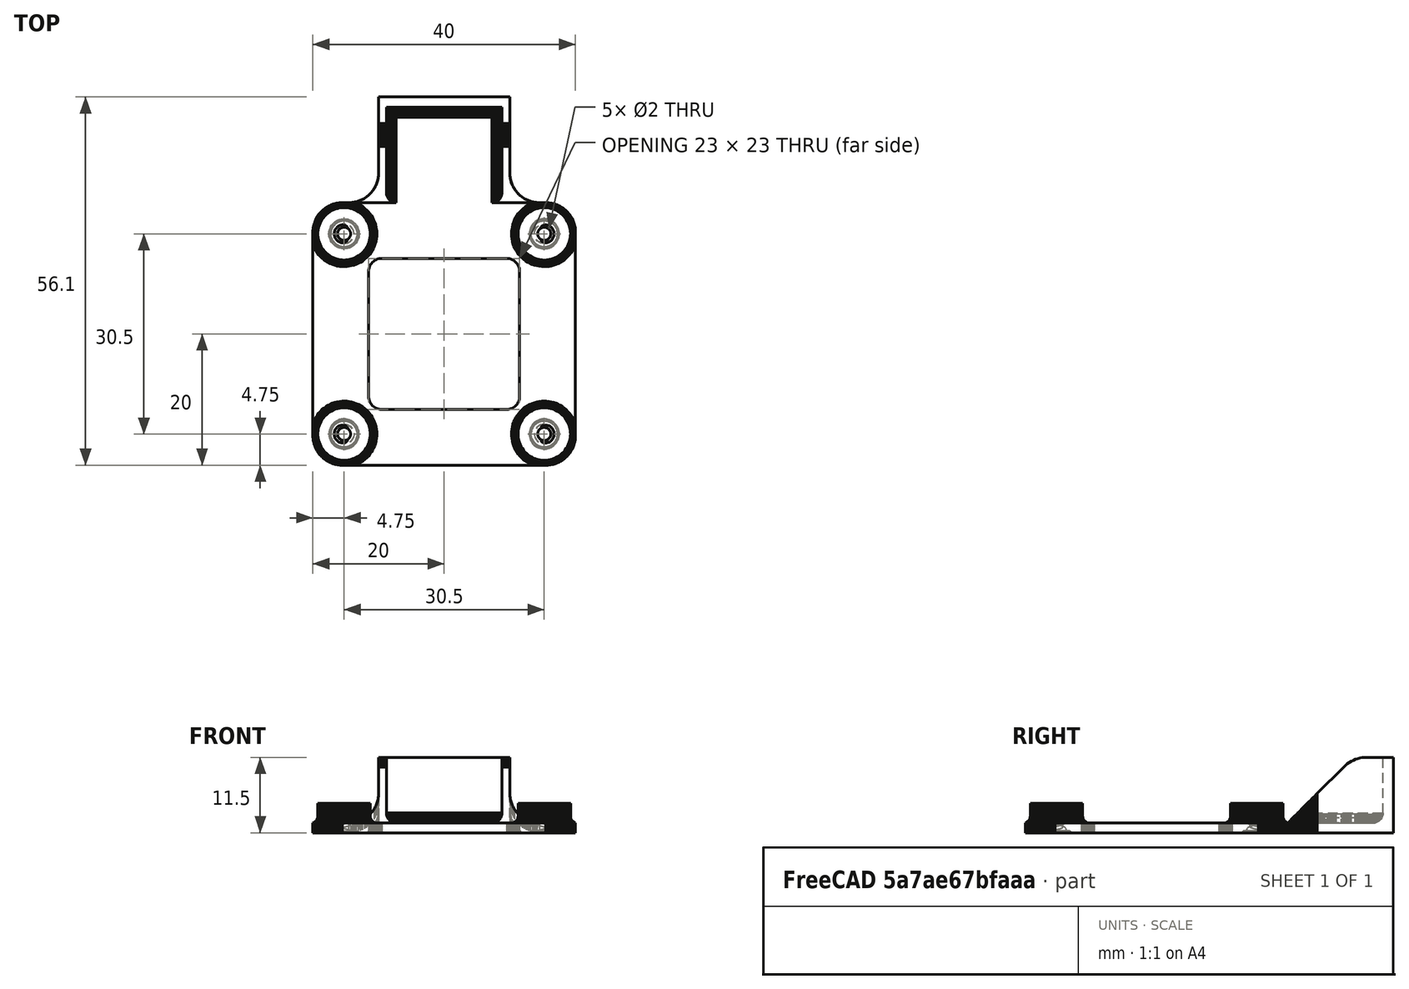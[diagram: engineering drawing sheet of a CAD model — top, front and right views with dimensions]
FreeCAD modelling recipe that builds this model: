
FCSTD DOCUMENT  (FreeCAD 0.21R33694 (Git))
Label: soporte-pdb
License: Creative Commons Attribution-NonCommercial-ShareAlike 4.0
LicenseURL: https://creativecommons.org/licenses/by-nc-sa/4.0/
objects: Part::Fuse×5, Part::Mirroring×4, Part::Feature×2, Part::Cylinder×1, Part::Refine×1, PartDesign::FeatureBase×1, PartDesign::Body×1, Part::Cut×1
note: 16 computed .brp shape members not serialized (recipe doc carries the construction recipe); baked Part::Feature solids carry a one-line shape summary decoded from their .brp

FEATURE [Part::Feature] Fusion001001  label="Rosca macho002"
  Placement = pos=(15.25,-15.25,3) rot=(0,0,1;0rad)
  shape: bbox 3.919 x 4.387 x 44 mm, 35 faces (baked)
FEATURE [Part::Cylinder] Cylinder
  Angle = 360
  AttacherType = Attacher::AttachEngine3D
  FirstAngle = 0
  Height = 4.5
  Placement = pos=(15.25,-15.25,0) rot=(0,0,1;0rad)
  Radius = 2
  SecondAngle = 0
FEATURE [Part::Mirroring] Part__Mirroring  label="Cylinder (Mirror #1)"
  Base = (0,0,0)
  Normal = (0,1,0)
  Source = -> Cylinder
FEATURE [Part::Fuse] Fusion
  Base = -> Cylinder
  Refine = true
  Tool = -> Part__Mirroring
FEATURE [Part::Mirroring] Part__Mirroring001  label="Fusion (Mirror #2)"
  Base = (0,0,0)
  Normal = (1,0,0)
  Source = -> Fusion
FEATURE [Part::Fuse] Fusion001002
  Base = -> Fusion
  Refine = true
  Tool = -> Part__Mirroring001
FEATURE [Part::Feature] base001_solid  label="base001 (Solid)"
  shape: bbox 40 x 56.1 x 11.5 mm, 10680 faces (baked)
FEATURE [Part::Refine] base001_solid001  label="base001 (Solid)001"
  Source = -> base001_solid
FEATURE [PartDesign::FeatureBase] BaseFeature
  BaseFeature = -> base001_solid001
FEATURE [PartDesign::Body] Body
  BaseFeature = -> base001_solid001
  Group = -> [BaseFeature]
  Origin = -> Origin
  Tip = -> BaseFeature
FEATURE [Part::Fuse] Fusion001003  label="soporte-pdb"
  Base = -> Fusion001002
  Refine = true
  Tool = -> Body
FEATURE [Part::Mirroring] Part__Mirroring002  label="Rosca macho002 (Mirror #3)"
  Base = (0,0,0)
  Normal = (0,1,0)
  Source = -> Fusion001001
FEATURE [Part::Fuse] Fusion001004
  Base = -> Fusion001001
  Refine = true
  Tool = -> Part__Mirroring002
FEATURE [Part::Mirroring] Part__Mirroring003  label="Fusion001004 (Mirror #4)"
  Base = (0,0,0)
  Normal = (1,0,0)
  Source = -> Fusion001004
FEATURE [Part::Fuse] Fusion001005
  Base = -> Fusion001004
  Placement = pos=(0,0,-3) rot=(0,0,1;0rad)
  Refine = true
  Tool = -> Part__Mirroring003
FEATURE [Part::Cut] Cut  label="soporte-pdb001"
  Base = -> Fusion001003
  Refine = true
  Tool = -> Fusion001005
